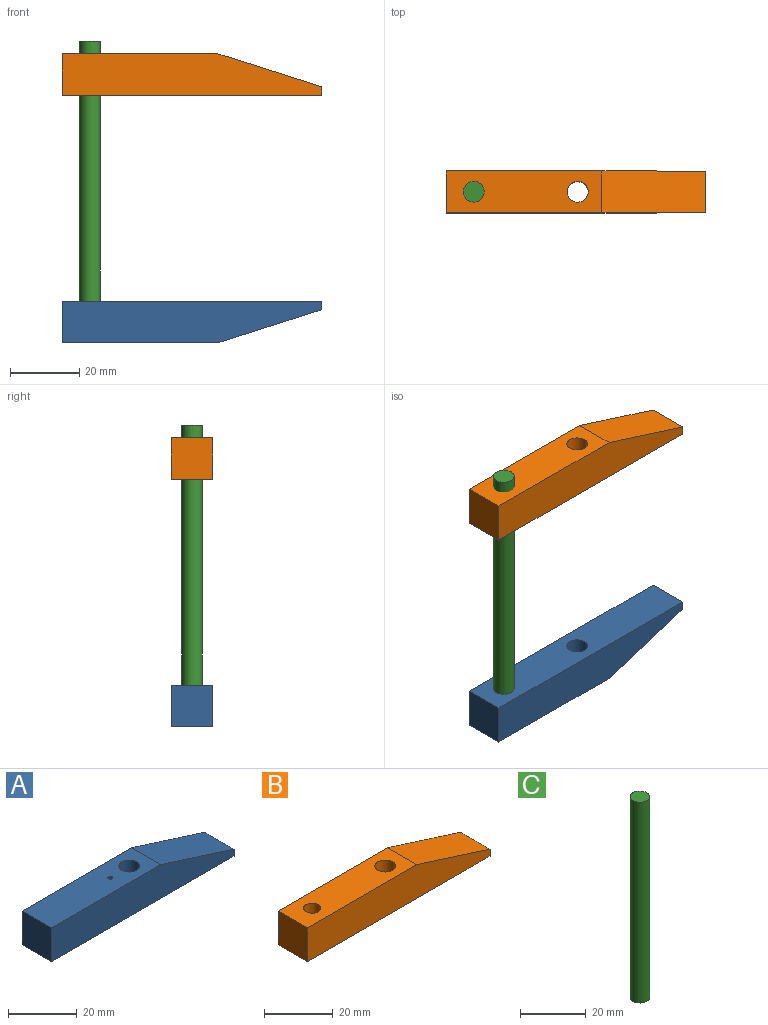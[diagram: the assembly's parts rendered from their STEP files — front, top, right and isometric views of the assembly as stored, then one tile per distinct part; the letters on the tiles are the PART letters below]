
ASSEMBLY  parts=3 mates=2
PART A: 12 faces, bbox 75x12x12 mm
  f0: plane 30x12mm, normal (0.3,0,0.95), area 377.6mm2, adj f1,f4,f5,f6
  f1: plane 45x12mm, normal (0,0,1), area 510mm2, adj f0,f2,f5,f6,f7,f8
  f2: plane 12x12mm, normal (-1,0,0), area 144mm2, adj f1,f3,f5,f6
  f3: plane 75x12mm, normal (0,0,-1), area 852.1mm2, adj f2,f4,f5,f6,f7,f10
  f4: plane 12x2.5mm, normal (1,0,0), area 30mm2, adj f0,f3,f5,f6
  f5: plane 75x12mm, normal (0,-1,0), area 757.5mm2, adj f0,f1,f2,f3,f4
  f6: plane 75x12mm, normal (0,1,0), area 757.5mm2, adj f0,f1,f2,f3,f4
  f7: cylinder r=3mm len=12mm, axis (0,0,1), area 226.2mm2, adj f1,f3
  f8: cylinder r=0.75mm len=6mm, axis (0,0,1), area 28.3mm2, adj f1,f9
  f9: plane 1.5x1.5mm, normal (0,0,1), area 1.8mm2, adj f8
  f10: cylinder r=2.5mm len=5mm, axis (0,0,-1), area 62.8mm2, adj f3,f11
  f11: plane 5x5mm, normal (0,0,-1), area 19.6mm2, adj f10
PART B: 9 faces, bbox 75x12x12 mm
  f0: plane 30x12mm, normal (0.3,0,0.95), area 377.6mm2, adj f1,f4,f5,f6
  f1: plane 45x12mm, normal (0,0,1), area 492.1mm2, adj f0,f2,f5,f6,f7,f8
  f2: plane 12x12mm, normal (-1,0,0), area 144mm2, adj f1,f3,f5,f6
  f3: plane 75x12mm, normal (0,0,-1), area 852.1mm2, adj f2,f4,f5,f6,f7,f8
  f4: plane 12x2.5mm, normal (1,0,0), area 30mm2, adj f0,f3,f5,f6
  f5: plane 75x12mm, normal (0,-1,0), area 757.5mm2, adj f0,f1,f2,f3,f4
  f6: plane 75x12mm, normal (0,1,0), area 757.5mm2, adj f0,f1,f2,f3,f4
  f7: cylinder r=3mm len=12mm, axis (0,0,1), area 226.2mm2, adj f1,f3
  f8: cylinder r=2.5mm len=12mm, axis (0,0,1), area 188.5mm2, adj f1,f3
PART C: 3 faces, bbox 6x6x75 mm
  f0: cylinder r=3mm len=75mm, axis (0,0,-1), area 1413.7mm2, adj f1,f2
  f1: plane 6x6mm, normal (0,0,1), area 28.3mm2, adj f0
  f2: plane 6x6mm, normal (0,0,-1), area 28.3mm2, adj f0
PLACE A rot(axis=(1,0,0),180deg) t=(1.47,23.84,-55.31)mm
PLACE B t=(1.47,35.84,4.11)mm
PLACE C rot(axis=(1,0,0),180deg) t=(-6.77,58.42,19.69)mm
MATE fastened A.f10 <-> C.f0  axis (0,0,1) through (-35.53,29.84,-55.31)mm
MATE slider C.f0 <-> B.f8  axis (0,0,1) through (-35.53,29.84,19.69)mm
